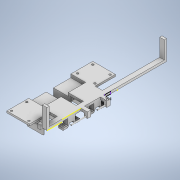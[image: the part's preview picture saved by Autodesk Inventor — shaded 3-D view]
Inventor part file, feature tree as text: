
AUTODESK INVENTOR PART (.ipt)
format: ipt  version: 2020.2 (Build 242310000, 310)  size: 723,968 bytes
history: native  units: mm
features: sketch x36, extrude x35, projected_geometry x10, hole x3
ambient origin geometry x8: Origin, YZ Plane, XZ Plane, XY Plane, X Axis, Y Axis, Z Axis, Center Point
bodies: Solid1 (feature_tree)
feature tree (84):
  sketch  "Sketch1"  dims[d0=8.0mm d1=116.7892mm]
  extrude  "Extrusion1"  Depth=116.7892mm
  extrude  "Extrusion2"  Depth=4.0mm
  extrude  "Extrusion3"  Depth=4.0mm TaperAngle=0.0deg
  extrude  "Extrusion4"  Depth=34.0mm
  extrude  "Extrusion5"  Depth=12.7mm
  extrude  "Extrusion6"  Depth=25.0mm
  hole  "Hole1"  [1 undecoded]
  extrude  "Extrusion11"  TaperAngle=60.0deg  [1 undecoded]
  extrude  "Extrusion12"  TaperAngle=120.0deg  [1 undecoded]
  sketch  "Sketch16"  dims[d19=6.4262mm d20=120.0deg]
  extrude  "Extrusion13"  Depth=6.4262mm
  extrude  "Extrusion14"  Depth=6.4262mm
  sketch  "Sketch17"  dims[d21=120.0deg d22=6.4262mm]
  extrude  "Extrusion15"  Depth=25.4mm TaperAngle=0.0deg
  extrude  "Extrusion18"  Depth=6.0mm
  extrude  "Extrusion19"  Depth=8.89mm
  extrude  "Extrusion20"  Depth=10.0mm
  hole  "Hole2"  [1 undecoded]
  extrude  "Extrusion21"  Depth=2.0mm
  extrude  "Extrusion22"  Depth=2.0mm
  sketch  "Sketch27"  dims[d45=8.89mm d46=2.0mm]
  extrude  "Extrusion23"  Depth=25.4mm
  extrude  "Extrusion24"  Depth=32.48mm
  extrude  "Extrusion25"  TaperAngle=90.0deg  [1 undecoded]
  sketch  "Sketch29"  dims[d79=51.53mm d80=32.48mm]
  extrude  "Extrusion26"  Depth=2.0mm
  extrude  "Extrusion27"  Depth=29.0mm
  extrude  "Extrusion28"  Depth=36.0mm TaperAngle=0.0deg
  sketch  "Sketch31"  dims[d83=4.0mm d84=0.0mm d87=2.0mm]
  extrude  "Extrusion29"  Depth=8.0mm
  extrude  "Extrusion30"  Depth=17.5mm
  extrude  "Extrusion31"  Depth=35.0mm
  extrude  "Extrusion32"  Depth=5.0mm
  extrude  "Extrusion33"  TaperAngle=90.0deg  [1 undecoded]
  extrude  "Extrusion34"  Depth=5.0mm
  extrude  "Extrusion35"  Depth=25.4mm TaperAngle=0.0deg
  extrude  "Extrusion37"  Depth=1.0mm
  extrude  "Extrusion38"  TaperAngle=0.0deg  [1 undecoded]
  extrude  "Extrusion39"  Depth=28.8036mm
  extrude  "Extrusion40"  Depth=25.4mm
  hole  "Hole4"  [1 undecoded]
  extrude  "Extrusion41"  Depth=25.4mm
  extrude  "Extrusion42"  Depth=6.4262mm
  sketch  "Sketch2"  dims[d2=8.0mm d3=4.0mm]
  sketch  "Sketch3"  dims[d4=4.0mm d5=4.0mm d6=0.0mm]
  sketch  "Sketch4"  dims[d7=34.0mm d8=0.0mm d9=19.558mm]
  sketch  "Sketch5"  dims[d10=16.1125mm d11=12.7mm]
  sketch  "Sketch6"  dims[d12=25.0mm d13=0.0mm d14=11.1125mm]
  sketch  "Sketch14"  dims[d15=6.4135mm d16=12.827mm]
  projected_geometry  "Projected Loop2"
  sketch  "Sketch15"  dims[d17=6.4262mm d18=60.0deg]
  projected_geometry  "Projected Loop3"
  sketch  "Sketch18"  dims[d23=120.0deg d24=6.4262mm]
  sketch  "Sketch21"  dims[d25=120.0deg d26=25.4mm d27=0.0mm]
  sketch  "Sketch22"  dims[d28=6.0mm d29=8.89mm]
  sketch  "Sketch23"  dims[d30=5.9944mm d31=8.89mm]
  sketch  "Sketch24"  dims[d32=25.4mm d33=0.0mm d34=10.0mm]
  sketch  "Sketch25"  dims[d35=90.0deg d36=20.0mm]
  projected_geometry  "Projected Loop5"
  sketch  "Sketch26"  dims[d37=3.4mm d38=19.05mm d39=6.2992mm d40=6.35mm d41=90.0deg d42=5.0mm d43=0.0mm d44=2.0mm]
  sketch  "Sketch28"  dims[d47=25.4mm d48=0.0mm d78=16.24mm]
  sketch  "Sketch30"  dims[d81=90.0deg d82=90.0deg]
  sketch  "Sketch32"  dims[d88=2.0mm d89=29.0mm]
  projected_geometry  "Projected Loop6"
  sketch  "Sketch33"  dims[d90=2.0mm d91=36.0mm d92=0.0mm]
  projected_geometry  "Projected Loop7"
  sketch  "Sketch34"  dims[d93=13.878mm d94=8.0mm]
  sketch  "Sketch35"  dims[d95=180.0deg d96=17.5mm]
  projected_geometry  "Projected Loop8"
  sketch  "Sketch36"  dims[d97=90.0deg d98=35.0mm]
  sketch  "Sketch37"  dims[d99=3.5mm d100=5.0mm]
  sketch  "Sketch38"  dims[d101=7.0mm d102=90.0deg]
  sketch  "Sketch41"  dims[d103=5.0mm d104=3.4mm]
  sketch  "Sketch42"  dims[d105=3.4mm d106=25.4mm d107=0.0mm]
  sketch  "Sketch43"  dims[d108=6.4262mm d109=0.0mm d110=1.0mm]
  projected_geometry  "Projected Loop9"
  projected_geometry  "Projected Loop10"
  projected_geometry  "Projected Loop11"
  projected_geometry  "Projected Loop12"
  sketch  "Sketch44"  dims[d111=1.0mm d112=0.0mm d113=0.0mm]
  sketch  "Sketch45"  dims[d128=44.8mm d129=28.8036mm]
  sketch  "Sketch46"  dims[d130=25.4mm d131=0.0mm d132=3.2131mm]
  sketch  "Sketch47"  dims[d133=6.4262mm d134=120.0deg d135=3.2131mm d136=6.4262mm d137=120.0deg d138=25.4mm d139=0.0mm d140=8.001mm d141=13.8938mm d142=8.001mm d143=0.0mm d144=25.4mm d145=0.0mm d146=10.0mm d147=20.0mm d148=3.4mm d149=19.05mm d150=6.2992mm d151=6.35mm d152=90.0deg d153=5.0mm d154=0.0mm d155=16.2433mm d156=32.4866mm d157=51.5366mm d158=4.0mm d159=0.0mm d160=29.0068mm d161=2.0mm d162=2.0mm d163=2.0mm d164=2.0mm d165=36.0mm d166=0.0mm d167=7.0mm d168=5.0mm d169=5.0mm d170=17.5mm d171=35.0mm d172=3.4mm d173=3.4mm d174=5.0mm d175=0.0mm d176=5.0mm d177=0.0mm d178=1.0mm d179=1.0mm d180=25.4mm d181=0.0mm d182=19.05mm d183=10.0mm d184=5.08mm d185=4.0mm d186=0.0mm d187=10.0mm d188=0.0mm d189=2.0mm d190=2.0mm d191=25.4mm d192=0.0mm d193=10.0mm d194=30.0mm d195=0.0mm d196=80.5688mm d197=0.0mm d198=4.0mm d199=30.0mm d200=0.0mm d201=11.43mm d202=0.0mm d203=25.4mm d204=0.0mm d205=25.4mm d206=0.0mm d207=25.4mm d208=0.0mm d237=25.4mm d238=0.0mm d239=25.4mm d240=0.0mm d241=1.5mm d242=0.0mm d243=39.0mm d244=35.0mm d245=39.0mm d246=35.0mm d247=3.0mm d248=0.0mm d249=5.0mm d250=5.0mm d251=29.7mm d252=26.05mm d253=4.0mm d254=4.0mm d255=29.7mm d256=26.05mm d257=3.4mm d258=19.05mm d259=6.2992mm d260=6.35mm d261=90.0deg d262=25.4mm d263=20.594885mm d264=7.8mm d265=0.0mm d266=30.0mm d267=5.7mm d268=29.9974mm d269=25.4mm d270=0.0mm d214=12.7mm d215=0.872665mm d216=12.7mm d217=0.872665mm d228=12.7mm d229=0.872665mm d230=12.7mm d231=0.872665mm]
note: 8 required parameter values undecoded (feature->parameter linkage not recoverable at this tier; creation-order binding heuristic only, values carry confidence <= 0.55)
